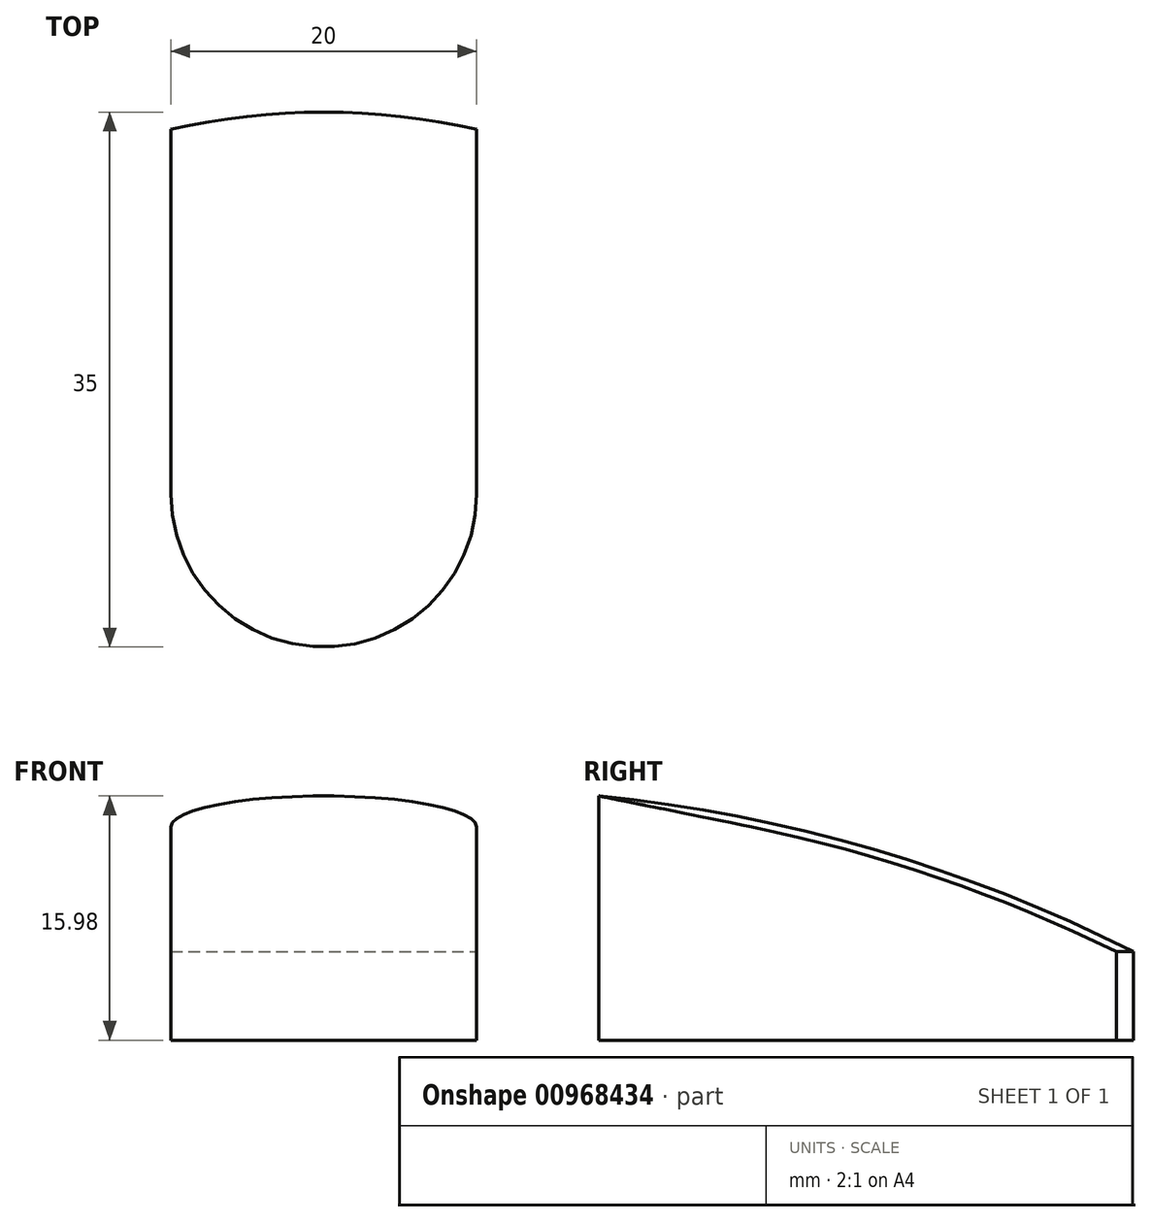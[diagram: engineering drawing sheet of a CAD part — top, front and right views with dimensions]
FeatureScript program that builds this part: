
annotation { "Feature Type Name" : "Feature", "Feature Type Description" : "" }
export const myFeature = defineFeature(function(context is Context, id is Id, definition is map)
    precondition{}
    {
        {
            var Q0;
            Q0=qCreatedBy(makeId("Top.planeOp"),FACE);
            var sketch = newSketch(context, id + "F0", { "sketchPlane" : qUnion([Q0])});
            skLineSegment(sketch, "E0", {"start": v(103.56, 20) * mm, "end": v(135, 20) * mm});
            skLineSegment(sketch, "E1", {"start": v(135, 20) * mm, "end": v(135, -20) * mm});
            skLineSegment(sketch, "E2", {"start": v(135, -20) * mm, "end": v(103.56, -20) * mm});
            skArc(sketch, "E3", {"start": v(62.14, 42) * mm, "mid": v(-75, 0) * mm, "end": v(62.14, -42) * mm});
            skArc(sketch, "E4.filletArc", {"start": v(62.14, 42) * mm, "mid": v(80.1, 25.84) * mm, "end": v(103.56, 20) * mm});
            skArc(sketch, "E5.filletArc", {"start": v(103.56, -20) * mm, "mid": v(80.1, -25.84) * mm, "end": v(62.14, -42) * mm});
            skArc(sketch, "E6", {"start": v(-10, 43.87) * mm, "mid": v(0, 45) * mm, "end": v(10, 43.87) * mm});
            skLineSegment(sketch, "E7", {"start": v(-10, 43.87) * mm, "end": v(-10, 20) * mm});
            skLineSegment(sketch, "E8", {"start": v(10, 43.87) * mm, "end": v(10, 20) * mm});
            skArc(sketch, "E9", {"start": v(-10, 20) * mm, "mid": v(0, 10) * mm, "end": v(10, 20) * mm});
            skSolve(sketch);
        }
        {
            var Q0;
            Q0=qCreatedBy(makeId("Front.planeOp"),FACE);
            var sketch = newSketch(context, id + "F1", { "sketchPlane" : qUnion([Q0])});
            skLineSegment(sketch, "E10", {"start": v(55, 0) * mm, "end": v(0, 0) * mm});
            skLineSegment(sketch, "E11", {"start": v(0, 0) * mm, "end": v(0, 16.48) * mm});
            skArc(sketch, "E12", {"start": v(55, 0) * mm, "mid": v(28.7, 12.27) * mm, "end": v(0, 16.48) * mm});
            skSolve(sketch);
        }
        {
            var Q0;
            Q0=makeQuery(id+"F0.imprint","IMPRINT",FACE,{"disambiguationData":[TD([[makeQuery(id+"F0.imprint","IMPRINT",EDGE,{"derivedFrom":sQuery(id+"F0.wireOp",EDGE,"E0")}),-1.0]])]});
            var Q1;
            Q1=makeQuery(id+"F0.imprint","IMPRINT",FACE,{"disambiguationData":[TD([[makeQuery(id+"F0.imprint","IMPRINT",EDGE,{"derivedFrom":sQuery(id+"F0.wireOp",EDGE,"E6")}),-1.0]])]});
            extrude(context, id + "F2", {"entities" : qUnion([Q0, Q1]), "oppositeDirection" : true, "depth" : 40 * mm, "offsetDistance" : 25 * mm});
        }
        {
            var Q0;
            Q0=makeQuery(id+"F2.opExtrude","SWEPT_FACE",FACE,{"disambiguationData":[OSD([sQuery(id+"F0.wireOp",EDGE,"E3")])]});
            fillet(context, id + "F3", {"entities" : qUnion([Q0]), "radius" : 20 * mm, "tangentPropagation" : true, "allowEdgeOverflow" : false});
        }
        {
            var Q0;
            Q0=makeQuery(id+"F1.imprint","IMPRINT",FACE,{"disambiguationData":[TD([[makeQuery(id+"F1.imprint","IMPRINT",EDGE,{"derivedFrom":sQuery(id+"F1.wireOp",EDGE,"E10")}),-1.0]])]});
            var Q1;
            Q1=sQuery(id+"F1.wireOp",EDGE,"E11");
            revolve(context, id + "F4", {"operationType" : NewBodyOperationType.ADD, "surfaceOperationType" : NewSurfaceOperationType.NEW, "entities" : qUnion([Q0]), "axis" : qUnion([Q1]), "revolveType" : RevolveType.FULL});
        }
        {
            var Q0;
            Q0=makeQuery(id+"F0.imprint","IMPRINT",FACE,{"disambiguationData":[TD([[makeQuery(id+"F0.imprint","IMPRINT",EDGE,{"derivedFrom":sQuery(id+"F0.wireOp",EDGE,"E6")}),-1.0]])]});
            extrude(context, id + "F5", {"entities" : qUnion([Q0]), "operationType" : NewBodyOperationType.REMOVE, "endBound" : BoundingType.THROUGH_ALL, "oppositeDirection" : true, "depth" : 25 * mm, "offsetDistance" : 25 * mm, "hasSecondDirection" : true, "secondDirectionBound" : BoundingType.THROUGH_ALL, "secondDirectionOppositeDirection" : false, "secondDirectionDepth" : 25 * mm});
        }
    });
